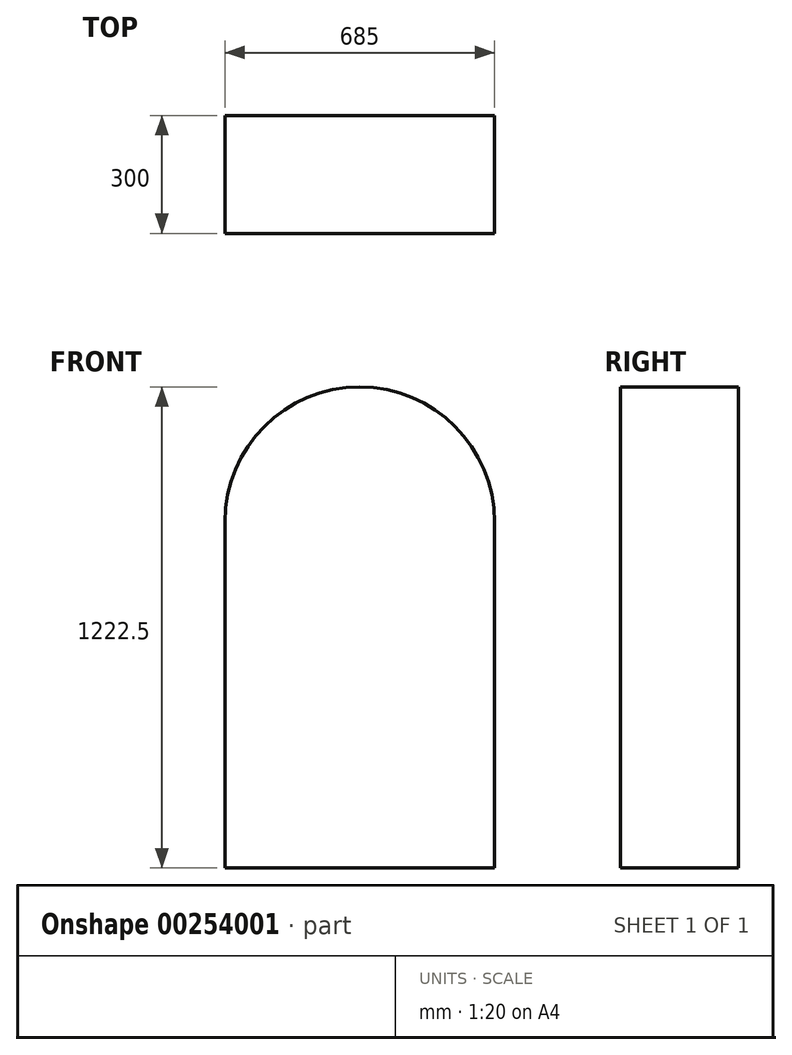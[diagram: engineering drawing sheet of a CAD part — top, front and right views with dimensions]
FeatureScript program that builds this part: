
annotation { "Feature Type Name" : "Feature", "Feature Type Description" : "" }
export const myFeature = defineFeature(function(context is Context, id is Id, definition is map)
    precondition{}
    {
        {
            var Q0;
            Q0=qCreatedBy(makeId("Front.planeOp"),FACE);
            var sketch = newSketch(context, id + "F0", { "sketchPlane" : qUnion([Q0])});
            skCircle(sketch, "E0", {"center": v(0, 0) * mm, "radius": 342.5 * mm});
            skLineSegment(sketch, "E1.bottom", {"start": v(-342.5, 0) * mm, "end": v(342.5, 0) * mm});
            skLineSegment(sketch, "E1.top", {"start": v(-342.5, -880) * mm, "end": v(342.5, -880) * mm});
            skLineSegment(sketch, "E1.left", {"start": v(-342.5, 0) * mm, "end": v(-342.5, -880) * mm});
            skLineSegment(sketch, "E1.right", {"start": v(342.5, 0) * mm, "end": v(342.5, -880) * mm});
            skSolve(sketch);
        }
        {
            var Q0;
            Q0 = qSketchRegion(id + "F0", true);
            extrude(context, id + "F1", {"entities" : qUnion([Q0]), "depth" : 300 * mm});
        }
    });
